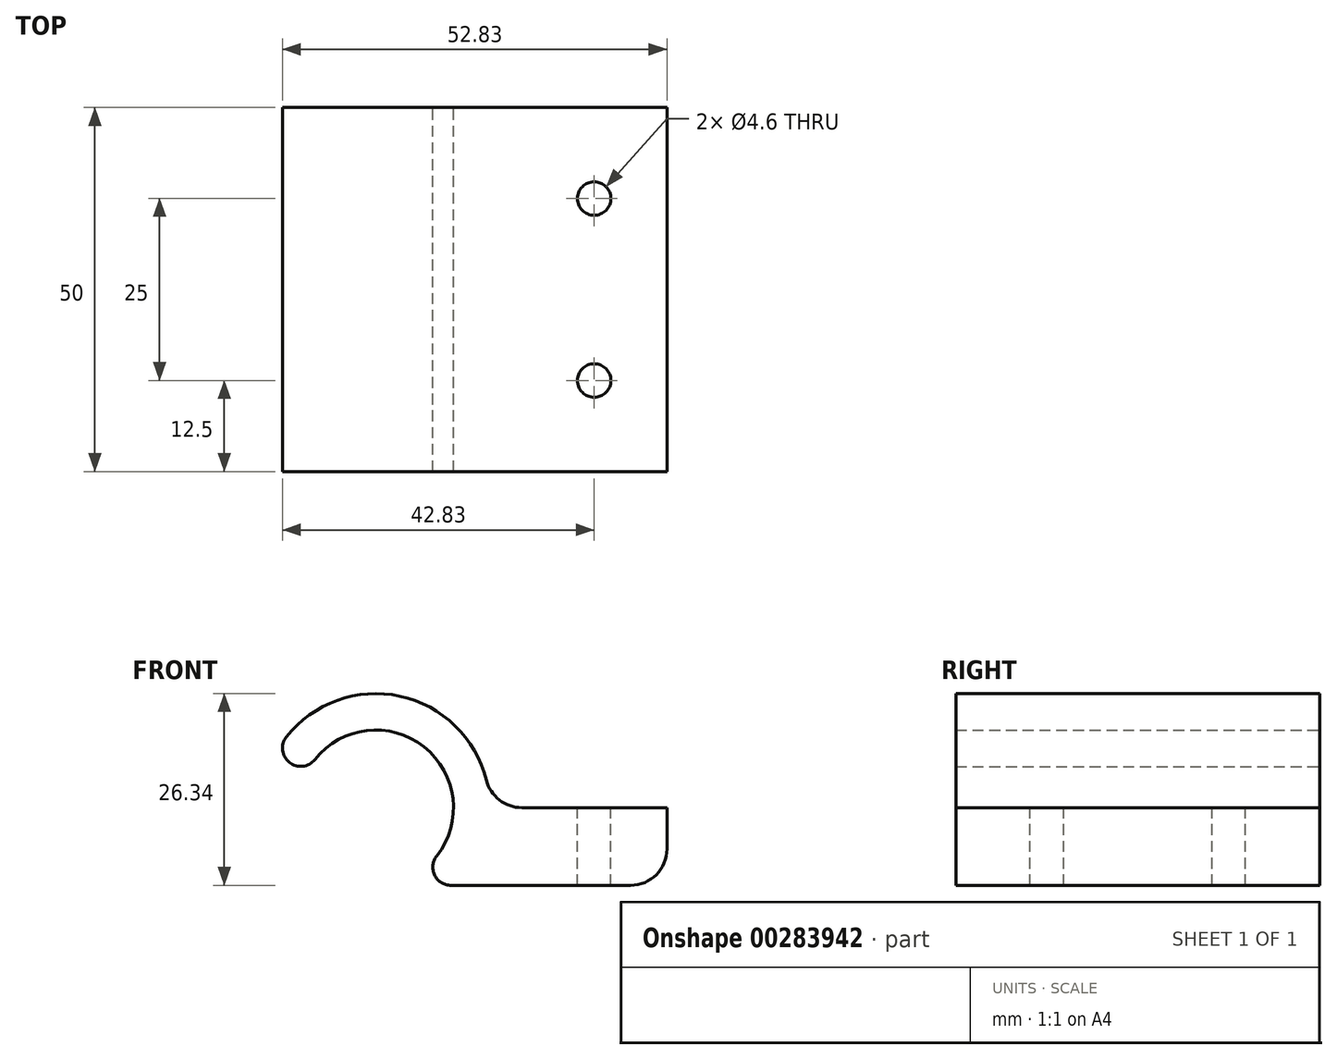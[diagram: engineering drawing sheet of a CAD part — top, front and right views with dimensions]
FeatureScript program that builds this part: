
annotation { "Feature Type Name" : "Feature", "Feature Type Description" : "" }
export const myFeature = defineFeature(function(context is Context, id is Id, definition is map)
    precondition{}
    {
        {
            var Q0;
            Q0=qCreatedBy(makeId("Front.planeOp"),FACE);
            var sketch = newSketch(context, id + "F0", { "sketchPlane" : qUnion([Q0])});
            skCircle(sketch, "E0", {"center": v(0, 0) * mm, "radius": 10.67 * mm, "construction": true});
            skLineSegment(sketch, "E1", {"start": v(0, 0) * mm, "end": v(52.75, 0) * mm, "construction": true});
            skArc(sketch, "E2", {"start": v(8.37, -6.62) * mm, "mid": v(6.62, 8.37) * mm, "end": v(-8.37, 6.62) * mm});
            skArc(sketch, "E3", {"start": v(-12.29, 9.72) * mm, "mid": v(-11.88, 6.2) * mm, "end": v(-8.37, 6.62) * mm});
            skArc(sketch, "E4", {"start": v(8.37, -6.62) * mm, "mid": v(8.08, -9.26) * mm, "end": v(10.33, -10.67) * mm});
            skLineSegment(sketch, "E5", {"start": v(0, 0) * mm, "end": v(0, -10.67) * mm, "construction": true});
            skLineSegment(sketch, "E6", {"start": v(0, -10.67) * mm, "end": v(62.64, -10.67) * mm, "construction": true});
            skCircle(sketch, "E7", {"center": v(0, 0) * mm, "radius": 15.67 * mm, "construction": true});
            skLineSegment(sketch, "E8", {"start": v(10.33, -8.17) * mm, "end": v(0, 0) * mm, "construction": true});
            skLineSegment(sketch, "E9", {"start": v(-10.33, 8.17) * mm, "end": v(0, 0) * mm, "construction": true});
            skLineSegment(sketch, "E10", {"start": v(40, 0) * mm, "end": v(40, -10.67) * mm});
            skLineSegment(sketch, "E11", {"start": v(40, -10.67) * mm, "end": v(10.33, -10.67) * mm});
            skArc(sketch, "E12", {"start": v(-12.29, 9.72) * mm, "mid": v(5.14, 14.8) * mm, "end": v(15.67, 0) * mm});
            skLineSegment(sketch, "E13", {"start": v(15.67, 0) * mm, "end": v(40, 0) * mm});
            skSolve(sketch);
        }
        {
            var Q0;
            Q0=qSketchRegion(id+"F0",true);
            extrude(context, id + "F1", {"entities" : qUnion([Q0]), "endBound" : BoundingType.SYMMETRIC, "depth" : 50 * mm});
        }
        {
            var Q0;
            Q0=makeQuery(id+"F1.opExtrude","SWEPT_EDGE",EDGE,{"disambiguationData":[OSD([sQuery(id+"F0.wireOp",EDGE,"E12"),sQuery(id+"F0.wireOp",EDGE,"E13")])]});
            var Q1;
            Q1=makeQuery(id+"F1.opExtrude","SWEPT_EDGE",EDGE,{"disambiguationData":[OSD([sQuery(id+"F0.wireOp",EDGE,"E10"),sQuery(id+"F0.wireOp",EDGE,"E11")])]});
            fillet(context, id + "F2", {"entities" : qUnion([Q0, Q1]), "radius" : 5 * mm, "tangentPropagation" : true, "allowEdgeOverflow" : false});
        }
        {
            var Q0;
            Q0=qCreatedBy(makeId("Top.planeOp"),FACE);
            var sketch = newSketch(context, id + "F3", { "sketchPlane" : qUnion([Q0])});
            skLineSegment(sketch, "E14", {"start": v(0, 0) * mm, "end": v(30, 0) * mm, "construction": true});
            skLineSegment(sketch, "E15", {"start": v(30, 0) * mm, "end": v(30, 12.5) * mm, "construction": true});
            skCircle(sketch, "E16", {"center": v(30, 12.5) * mm, "radius": 2.3 * mm});
            skCircle(sketch, "E17.MirrorC", {"center": v(30, -12.5) * mm, "radius": 2.3 * mm});
            skSolve(sketch);
        }
        {
            var Q0;
            Q0=qSketchRegion(id+"F3",true);
            extrude(context, id + "F4", {"entities" : qUnion([Q0]), "operationType" : NewBodyOperationType.REMOVE, "endBound" : BoundingType.THROUGH_ALL, "oppositeDirection" : true, "depth" : 25 * mm});
        }
    });
